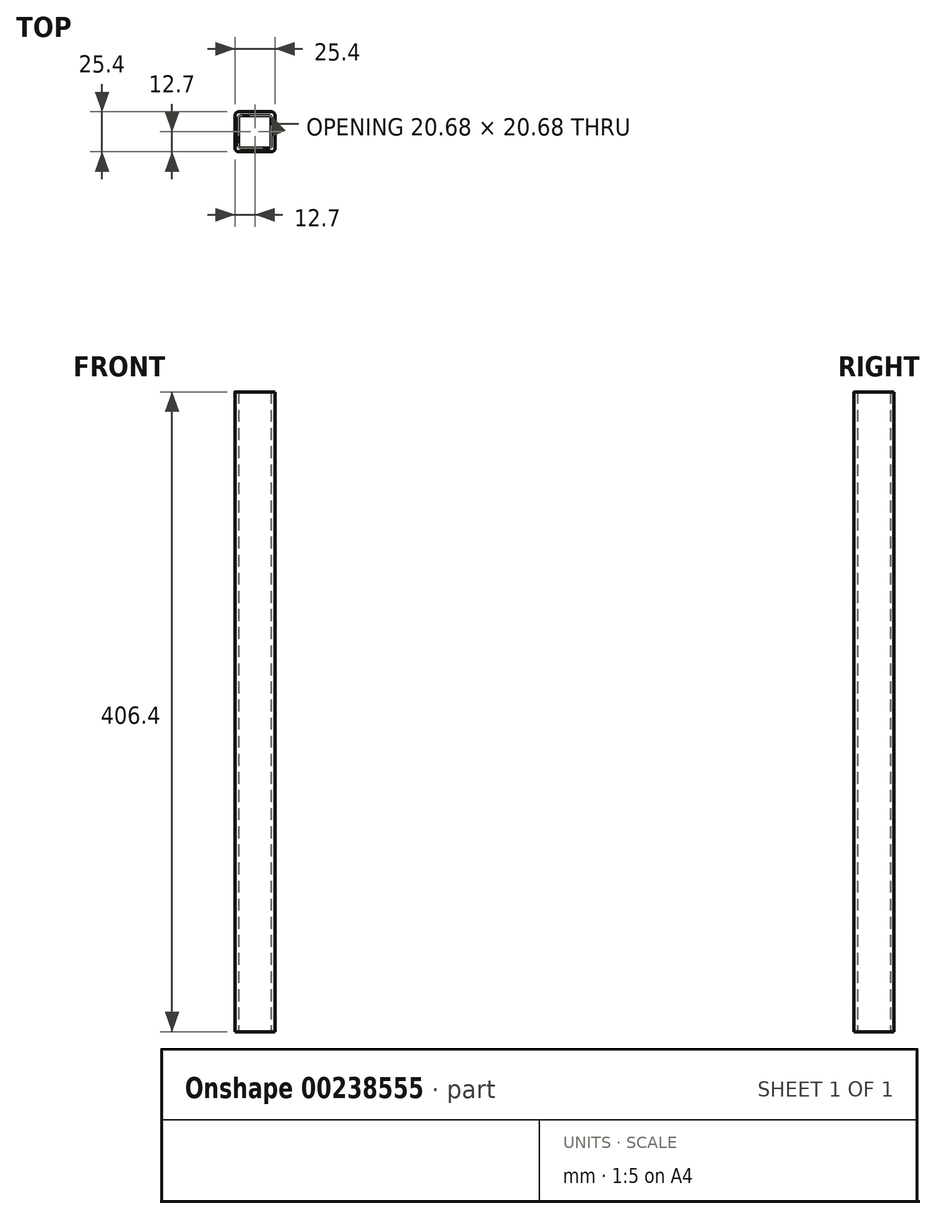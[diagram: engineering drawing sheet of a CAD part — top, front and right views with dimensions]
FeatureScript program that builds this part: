
annotation { "Feature Type Name" : "Feature", "Feature Type Description" : "" }
export const myFeature = defineFeature(function(context is Context, id is Id, definition is map)
    precondition{}
    {
        {
            var Q0;
            Q0=qCreatedBy(makeId("Top.planeOp"),FACE);
            var sketch = newSketch(context, id + "F0", { "sketchPlane" : qUnion([Q0])});
            skLineSegment(sketch, "E0", {"start": v(-12.7, 10.34) * mm, "end": v(-12.7, -10.34) * mm});
            skLineSegment(sketch, "E1", {"start": v(-10.34, -12.7) * mm, "end": v(10.34, -12.7) * mm});
            skLineSegment(sketch, "E2", {"start": v(12.7, -10.34) * mm, "end": v(12.7, 10.34) * mm});
            skLineSegment(sketch, "E3", {"start": v(10.34, 12.7) * mm, "end": v(-10.34, 12.7) * mm});
            skLineSegment(sketch, "E4", {"start": v(0, 12.7) * mm, "end": v(0, -12.7) * mm, "construction": true});
            skLineSegment(sketch, "E5", {"start": v(-12.7, 0) * mm, "end": v(12.7, 0) * mm, "construction": true});
            skPoint(sketch, "E6", {"position": v(0, 0) * mm});
            skPoint(sketch, "E7.visualSharp", {"position": v(-12.7, 12.7) * mm});
            skArc(sketch, "E7.filletArc", {"start": v(-10.34, 12.7) * mm, "mid": v(-12, 12) * mm, "end": v(-12.7, 10.34) * mm});
            skPoint(sketch, "E8.visualSharp", {"position": v(12.7, 12.7) * mm});
            skArc(sketch, "E8.filletArc", {"start": v(12.7, 10.34) * mm, "mid": v(12, 12) * mm, "end": v(10.34, 12.7) * mm});
            skPoint(sketch, "E9.visualSharp", {"position": v(12.7, -12.7) * mm});
            skArc(sketch, "E9.filletArc", {"start": v(10.34, -12.7) * mm, "mid": v(12, -12) * mm, "end": v(12.7, -10.34) * mm});
            skPoint(sketch, "E10.visualSharp", {"position": v(-12.7, -12.7) * mm});
            skArc(sketch, "E10.filletArc", {"start": v(-12.7, -10.34) * mm, "mid": v(-12, -12) * mm, "end": v(-10.34, -12.7) * mm});
            skLineSegment(sketch, "E11.0", {"start": v(8.81, 10.34) * mm, "end": v(-8.81, 10.34) * mm});
            skLineSegment(sketch, "E12.0", {"start": v(10.34, -8.81) * mm, "end": v(10.34, 8.81) * mm});
            skLineSegment(sketch, "E13.0", {"start": v(-8.81, -10.34) * mm, "end": v(8.81, -10.34) * mm});
            skLineSegment(sketch, "E14.0", {"start": v(-10.34, 8.81) * mm, "end": v(-10.34, -8.81) * mm});
            skArc(sketch, "E15.filletArc", {"start": v(-8.81, 10.34) * mm, "mid": v(-9.9, 9.9) * mm, "end": v(-10.34, 8.81) * mm});
            skArc(sketch, "E16.filletArc", {"start": v(10.34, 8.81) * mm, "mid": v(9.9, 9.9) * mm, "end": v(8.81, 10.34) * mm});
            skArc(sketch, "E17.filletArc", {"start": v(8.81, -10.34) * mm, "mid": v(9.9, -9.9) * mm, "end": v(10.34, -8.81) * mm});
            skArc(sketch, "E18.filletArc", {"start": v(-10.34, -8.81) * mm, "mid": v(-9.9, -9.9) * mm, "end": v(-8.81, -10.34) * mm});
            skSolve(sketch);
        }
        {
            var Q0;
            Q0=makeQuery(id+"F0.imprint","IMPRINT",FACE,{"disambiguationData":[TD([[makeQuery(id+"F0.imprint","IMPRINT",EDGE,{"derivedFrom":sQuery(id+"F0.wireOp",EDGE,"E0")}),1.0]])]});
            extrude(context, id + "F1", {"entities" : qUnion([Q0]), "depth" : 406.4 * mm});
        }
    });
